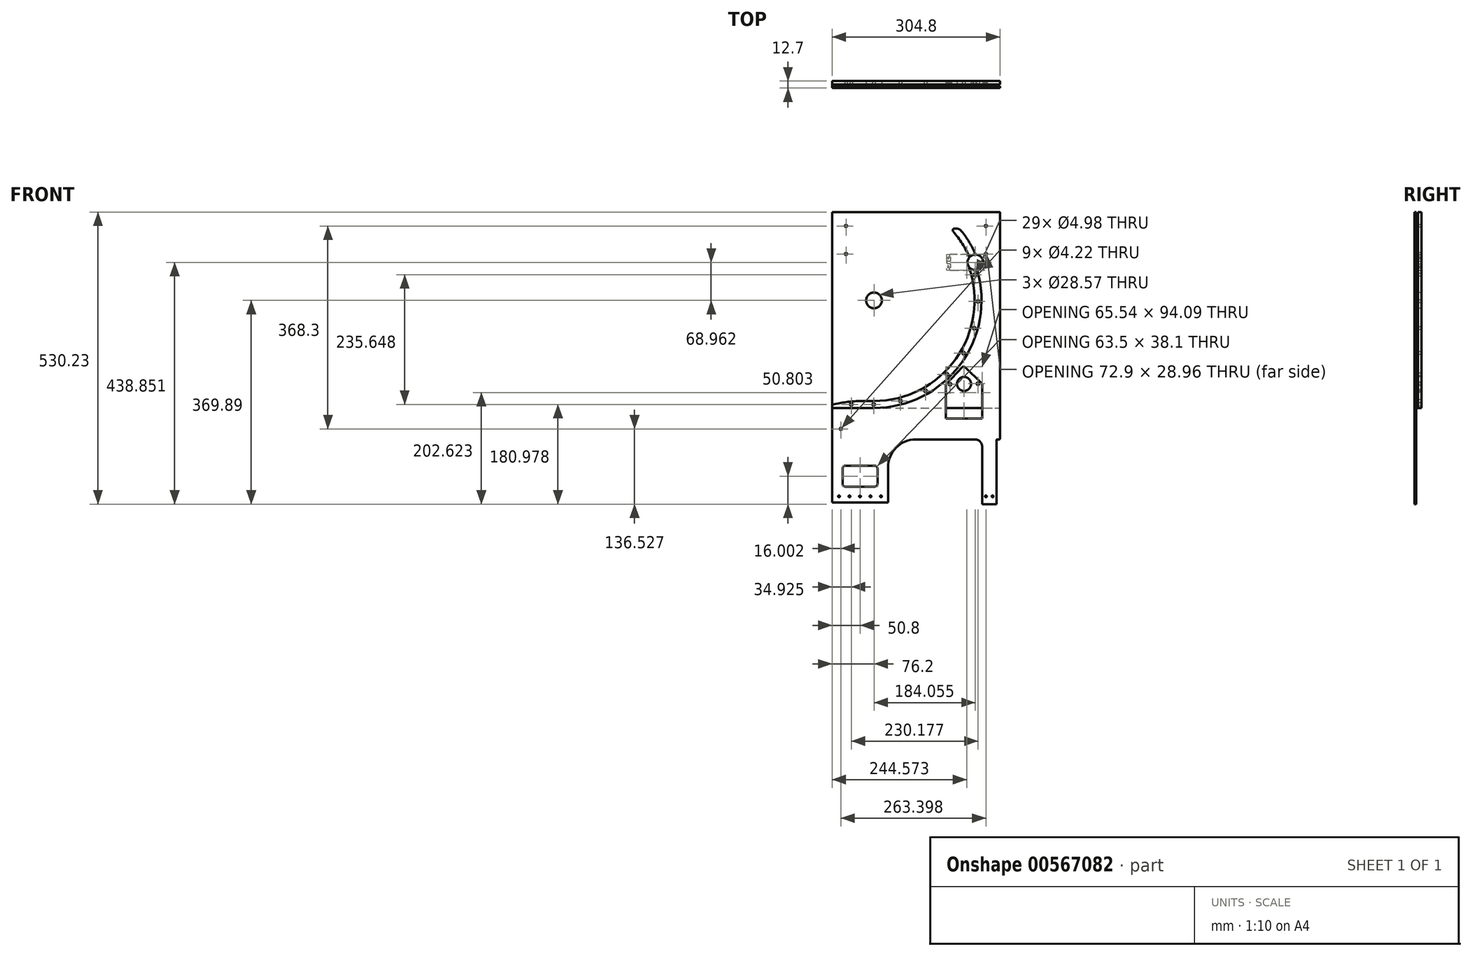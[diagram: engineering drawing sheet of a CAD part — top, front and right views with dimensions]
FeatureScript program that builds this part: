
annotation { "Feature Type Name" : "Feature", "Feature Type Description" : "" }
export const myFeature = defineFeature(function(context is Context, id is Id, definition is map)
    precondition{}
    {
        {
            var Q0;
            Q0=qCreatedBy(makeId("Front.planeOp"),FACE);
            var sketch = newSketch(context, id + "F0", { "sketchPlane" : qUnion([Q0])});
            skCircle(sketch, "E0", {"center": v(0, 0) * mm, "radius": 61.91 * mm, "construction": true});
            skArc(sketch, "E1", {"start": v(0, -182.56) * mm, "mid": v(148.63, -106.01) * mm, "end": v(172.62, 59.44) * mm});
            skLineSegment(sketch, "E2", {"start": v(228.6, -195.26) * mm, "end": v(228.6, 59.44) * mm, "construction": true});
            skLineSegment(sketch, "E3", {"start": v(228.6, 59.44) * mm, "end": v(172.62, 59.44) * mm});
            skLineSegment(sketch, "E4", {"start": v(0, 0) * mm, "end": v(182.56, 0) * mm, "construction": true});
            skLineSegment(sketch, "E5", {"start": v(0, 0) * mm, "end": v(172.62, 59.44) * mm, "construction": true});
            skLineSegment(sketch, "E6", {"start": v(209.55, -195.26) * mm, "end": v(209.55, 59.44) * mm, "construction": true});
            skPoint(sketch, "E7.middle", {"position": v(163.49, -151.68) * mm});
            skLineSegment(sketch, "E8.top", {"start": v(228.6, -195.26) * mm, "end": v(-76.2, -195.26) * mm});
            skLineSegment(sketch, "E8.right", {"start": v(-76.2, -188.91) * mm, "end": v(-76.2, -195.26) * mm});
            skLineSegment(sketch, "E9", {"start": v(0, -182.56) * mm, "end": v(-41.27, -182.56) * mm});
            skCircle(sketch, "E10", {"center": v(163.49, -151.68) * mm, "radius": 25.4 * mm, "construction": true});
            skLineSegment(sketch, "E11", {"start": v(130.72, -152.33) * mm, "end": v(162.84, -118.9) * mm, "construction": true});
            skLineSegment(sketch, "E12", {"start": v(162.84, -118.9) * mm, "end": v(196.26, -151.03) * mm, "construction": true});
            skLineSegment(sketch, "E13", {"start": v(196.26, -151.03) * mm, "end": v(164.14, -184.45) * mm, "construction": true});
            skLineSegment(sketch, "E14", {"start": v(164.14, -184.45) * mm, "end": v(130.72, -152.33) * mm, "construction": true});
            skLineSegment(sketch, "E15", {"start": v(162.84, -118.9) * mm, "end": v(164.14, -184.45) * mm, "construction": true});
            skCircle(sketch, "E16", {"center": v(183.04, 46.74) * mm, "radius": 2.49 * mm});
            skCircle(sketch, "E17.1.0", {"center": v(188.9, -2) * mm, "radius": 2.49 * mm});
            skCircle(sketch, "E17.2.0", {"center": v(182.01, -50.6) * mm, "radius": 2.49 * mm});
            skCircle(sketch, "E17.3.0", {"center": v(162.84, -95.77) * mm, "radius": 2.49 * mm});
            skCircle(sketch, "E17.4.0", {"center": v(132.67, -134.49) * mm, "radius": 2.49 * mm});
            skCircle(sketch, "E17.5.0", {"center": v(93.54, -164.13) * mm, "radius": 2.49 * mm});
            skCircle(sketch, "E17.6.0", {"center": v(48.1, -182.69) * mm, "radius": 2.49 * mm});
            skCircle(sketch, "E17.7.0", {"center": v(-0.58, -188.91) * mm, "radius": 2.49 * mm});
            skLineSegment(sketch, "E17.anchor1", {"start": v(0, 0) * mm, "end": v(183.04, 46.74) * mm, "construction": true});
            skLineSegment(sketch, "E17.anchor2", {"start": v(0, 0) * mm, "end": v(-0.58, -188.91) * mm, "construction": true});
            skLineSegment(sketch, "E18", {"start": v(130.72, -152.33) * mm, "end": v(130.72, -195.26) * mm, "construction": true});
            skLineSegment(sketch, "E19", {"start": v(196.26, -151.03) * mm, "end": v(196.26, -195.26) * mm, "construction": true});
            skCircle(sketch, "E20", {"center": v(-41.27, -188.91) * mm, "radius": 2.49 * mm});
            skLineSegment(sketch, "E21", {"start": v(-76.2, -188.91) * mm, "end": v(-41.27, -182.56) * mm});
            skArc(sketch, "E22.trimOffspring", {"start": v(0, -195.26) * mm, "mid": v(157.7, -115.16) * mm, "end": v(186, 59.44) * mm});
            skPoint(sketch, "E23.orphan", {"position": v(-76.2, -182.56) * mm});
            skSolve(sketch);
        }
        {
            var Q0;
            {var subQ1=sQuery(id+"F0.wireOp",EDGE,"E8.top");var subQ5=sQuery(id+"F0.wireOp",EDGE,"E8.right");var subQ6=makeQuery(id+"F0.imprint","INTERSECT",VERTEX,{"derivedFrom":[subQ1,subQ5]});Q0=makeQuery(id+"F0.imprint","IMPRINT",FACE,{"disambiguationData":[TD([[makeQuery(id+"F0.imprint","IMPRINT",EDGE,{"disambiguationData":[TD([[subQ6,1.0]])],"derivedFrom":subQ1}),-1.0]])]});}
            var Q1;
            {var subQ0=sQuery(id+"F0.wireOp",EDGE,"E1");Q1=makeQuery(id+"F0.imprint","IMPRINT",FACE,{"disambiguationData":[TD([[makeQuery(id+"F0.imprint","IMPRINT",EDGE,{"derivedFrom":subQ0}),-1.0]])]});}
            extrude(context, id + "F1", {"entities" : qUnion([Q0, Q1]), "depth" : 6.35 * mm, "offsetDistance" : 25.4 * mm});
        }
        {
            var Q0;
            {var subQ0=sQuery(id+"F0.wireOp",EDGE,"E1");Q0=makeQuery(id+"F0.imprint","IMPRINT",FACE,{"disambiguationData":[TD([[makeQuery(id+"F0.imprint","IMPRINT",EDGE,{"derivedFrom":subQ0}),-1.0]])]});}
            var sketch = newSketch(context, id + "F2", { "sketchPlane" : qUnion([Q0])});
            skCircle(sketch, "E24", {"center": v(0, 0) * mm, "radius": 14.29 * mm});
            skLineSegment(sketch, "E25.bottom", {"start": v(-76.2, -252.41) * mm, "end": v(228.6, -252.41) * mm});
            skLineSegment(sketch, "E25.top", {"start": v(-76.2, 160.34) * mm, "end": v(228.6, 160.34) * mm});
            skLineSegment(sketch, "E25.left", {"start": v(-76.2, -252.41) * mm, "end": v(-76.2, 160.34) * mm});
            skLineSegment(sketch, "E25.right", {"start": v(228.6, -252.41) * mm, "end": v(228.6, 160.34) * mm});
            skPoint(sketch, "E26.0", {"position": v(183.04, 46.74) * mm});
            skCircle(sketch, "E27.0", {"center": v(188.9, -2) * mm, "radius": 2.49 * mm});
            skCircle(sketch, "E27.1", {"center": v(183.04, 46.74) * mm, "radius": 2.49 * mm});
            skCircle(sketch, "E27.2", {"center": v(182.01, -50.6) * mm, "radius": 2.49 * mm});
            skCircle(sketch, "E27.3", {"center": v(162.84, -95.77) * mm, "radius": 2.49 * mm});
            skCircle(sketch, "E27.4", {"center": v(132.67, -134.49) * mm, "radius": 2.49 * mm});
            skCircle(sketch, "E27.5", {"center": v(93.54, -164.13) * mm, "radius": 2.49 * mm});
            skCircle(sketch, "E27.6", {"center": v(48.1, -182.69) * mm, "radius": 2.49 * mm});
            skCircle(sketch, "E27.7", {"center": v(-0.58, -188.91) * mm, "radius": 2.49 * mm});
            skCircle(sketch, "E27.8", {"center": v(-41.27, -188.91) * mm, "radius": 2.49 * mm});
            skCircle(sketch, "E28.0", {"center": v(163.49, -151.68) * mm, "radius": 25.4 * mm, "construction": true});
            skPoint(sketch, "E29.0", {"position": v(130.72, -152.33) * mm});
            skPoint(sketch, "E29.1", {"position": v(196.26, -151.03) * mm});
            skLineSegment(sketch, "E30", {"start": v(130.72, -152.33) * mm, "end": v(196.26, -151.03) * mm, "construction": true});
            skCircle(sketch, "E31", {"center": v(138.1, -152.18) * mm, "radius": 2.49 * mm});
            skCircle(sketch, "E32", {"center": v(188.88, -151.17) * mm, "radius": 2.49 * mm});
            skCircle(sketch, "E33", {"center": v(346.2, -207.96) * mm, "radius": 2.1 * mm});
            skLineSegment(sketch, "E34.bottom", {"start": v(-76.2, -195.26) * mm, "end": v(381, -195.26) * mm});
            skLineSegment(sketch, "E34.top", {"start": v(-76.2, -252.41) * mm, "end": v(381, -252.41) * mm});
            skLineSegment(sketch, "E34.left", {"start": v(-76.2, -195.26) * mm, "end": v(-76.2, -252.41) * mm});
            skLineSegment(sketch, "E34.right", {"start": v(381, -195.26) * mm, "end": v(381, -252.41) * mm});
            skCircle(sketch, "E35.0.1.0", {"center": v(346.2, -233.36) * mm, "radius": 2.1 * mm});
            skCircle(sketch, "E35.1.0.0", {"center": v(320.8, -207.96) * mm, "radius": 2.1 * mm});
            skCircle(sketch, "E35.1.1.0", {"center": v(320.8, -233.36) * mm, "radius": 2.1 * mm});
            skCircle(sketch, "E35.2.0.0", {"center": v(295.4, -207.96) * mm, "radius": 2.1 * mm});
            skCircle(sketch, "E35.2.1.0", {"center": v(295.4, -233.36) * mm, "radius": 2.1 * mm});
            skCircle(sketch, "E35.3.0.0", {"center": v(270, -207.96) * mm, "radius": 2.1 * mm});
            skCircle(sketch, "E35.3.1.0", {"center": v(270, -233.36) * mm, "radius": 2.1 * mm});
            skCircle(sketch, "E35.4.0.0", {"center": v(244.6, -207.96) * mm, "radius": 2.1 * mm});
            skCircle(sketch, "E35.4.1.0", {"center": v(244.6, -233.36) * mm, "radius": 2.1 * mm});
            skCircle(sketch, "E35.5.0.0", {"center": v(219.2, -207.96) * mm, "radius": 2.1 * mm});
            skCircle(sketch, "E35.5.1.0", {"center": v(219.2, -233.36) * mm, "radius": 2.1 * mm});
            skCircle(sketch, "E35.6.0.0", {"center": v(193.8, -207.96) * mm, "radius": 2.1 * mm});
            skCircle(sketch, "E35.6.1.0", {"center": v(193.8, -233.36) * mm, "radius": 2.1 * mm});
            skCircle(sketch, "E35.7.0.0", {"center": v(168.4, -207.96) * mm, "radius": 2.1 * mm});
            skCircle(sketch, "E35.7.1.0", {"center": v(168.4, -233.36) * mm, "radius": 2.1 * mm});
            skCircle(sketch, "E35.8.0.0", {"center": v(143, -207.96) * mm, "radius": 2.1 * mm});
            skCircle(sketch, "E35.8.1.0", {"center": v(143, -233.36) * mm, "radius": 2.1 * mm});
            skCircle(sketch, "E35.9.0.0", {"center": v(117.6, -207.96) * mm, "radius": 2.1 * mm});
            skCircle(sketch, "E35.9.1.0", {"center": v(117.6, -233.36) * mm, "radius": 2.1 * mm});
            skCircle(sketch, "E35.10.0.0", {"center": v(92.2, -207.96) * mm, "radius": 2.1 * mm});
            skCircle(sketch, "E35.10.1.0", {"center": v(92.2, -233.36) * mm, "radius": 2.1 * mm});
            skCircle(sketch, "E35.11.0.0", {"center": v(66.8, -207.96) * mm, "radius": 2.1 * mm});
            skCircle(sketch, "E35.11.1.0", {"center": v(66.8, -233.36) * mm, "radius": 2.1 * mm});
            skCircle(sketch, "E35.12.0.0", {"center": v(41.4, -207.96) * mm, "radius": 2.1 * mm});
            skCircle(sketch, "E35.12.1.0", {"center": v(41.4, -233.36) * mm, "radius": 2.1 * mm});
            skCircle(sketch, "E35.13.0.0", {"center": v(16, -207.96) * mm, "radius": 2.1 * mm});
            skCircle(sketch, "E35.13.1.0", {"center": v(16, -233.36) * mm, "radius": 2.1 * mm});
            skCircle(sketch, "E35.14.0.0", {"center": v(-9.4, -207.96) * mm, "radius": 2.1 * mm});
            skCircle(sketch, "E35.14.1.0", {"center": v(-9.4, -233.36) * mm, "radius": 2.1 * mm});
            skCircle(sketch, "E35.15.0.0", {"center": v(-34.8, -207.96) * mm, "radius": 2.1 * mm});
            skCircle(sketch, "E35.15.1.0", {"center": v(-34.8, -233.36) * mm, "radius": 2.1 * mm});
            skCircle(sketch, "E35.16.0.0", {"center": v(-60.2, -207.96) * mm, "radius": 2.1 * mm});
            skCircle(sketch, "E35.16.1.0", {"center": v(-60.2, -233.36) * mm, "radius": 2.1 * mm});
            skLineSegment(sketch, "E35.direction1", {"start": v(346.2, -207.96) * mm, "end": v(320.8, -207.96) * mm, "construction": true});
            skLineSegment(sketch, "E35.direction2", {"start": v(346.2, -207.96) * mm, "end": v(346.2, -233.36) * mm, "construction": true});
            skCircle(sketch, "E36", {"center": v(163.49, -151.68) * mm, "radius": 12.7 * mm});
            skLineSegment(sketch, "E37", {"start": v(-50.8, 160.34) * mm, "end": v(-50.8, -195.26) * mm, "construction": true});
            skCircle(sketch, "E38", {"center": v(-50.8, 84.14) * mm, "radius": 2.1 * mm});
            skCircle(sketch, "E39.0.1.0", {"center": v(-50.8, 134.94) * mm, "radius": 2.1 * mm});
            skLineSegment(sketch, "E39.direction1", {"start": v(-50.8, 84.14) * mm, "end": v(-50.8, 84.14) * mm});
            skLineSegment(sketch, "E39.direction2", {"start": v(-50.8, 84.14) * mm, "end": v(-50.8, 134.94) * mm, "construction": true});
            skLineSegment(sketch, "E40", {"start": v(76.2, 160.34) * mm, "end": v(76.2, -195.26) * mm, "construction": true});
            skCircle(sketch, "E41.MirrorC", {"center": v(203.2, 84.14) * mm, "radius": 2.1 * mm});
            skCircle(sketch, "E42.MirrorC", {"center": v(203.2, 134.94) * mm, "radius": 2.1 * mm});
            skLineSegment(sketch, "E43.MirrorCS", {"start": v(203.2, 84.14) * mm, "end": v(203.2, 134.94) * mm, "construction": true});
            skLineSegment(sketch, "E44.0", {"start": v(0, -182.56) * mm, "end": v(-41.27, -182.56) * mm});
            skSolve(sketch);
        }
        {
            var Q0;
            {var subQ3=sQuery(id+"F2.wireOp",EDGE,"E34.left");Q0=makeQuery(id+"F2.imprint","IMPRINT",FACE,{"disambiguationData":[TD([[makeQuery(id+"F2.imprint","IMPRINT",EDGE,{"derivedFrom":subQ3}),1.0]])]});}
            var Q1;
            Q1=makeQuery(id+"F2.imprint","IMPRINT",FACE,{"disambiguationData":[TD([[makeQuery(id+"F2.imprint","IMPRINT",EDGE,{"derivedFrom":sQuery(id+"F2.wireOp",EDGE,"E24")}),-1.0]])]});
            var Q2;
            Q2=makeQuery(id+"F2.imprint","IMPRINT",FACE,{"disambiguationData":[TD([[makeQuery(id+"F2.imprint","IMPRINT",EDGE,{"derivedFrom":sQuery(id+"F2.wireOp",EDGE,"E27.0")}),-1.0]])]});
            var Q3;
            {var subQ1=sQuery(id+"F0.wireOp",EDGE,"E21");var subQ2=makeQuery(id+"F0.imprint","INTERSECT",VERTEX,{"derivedFrom":[sQuery(id+"F0.wireOp",EDGE,"qDOghrOL-mCar-WwbD-ljMS-Sb26vS9t9zeY"),subQ1]});var subQ3=makeQuery(id+"F0.imprint","IMPRINT",EDGE,{"disambiguationData":[TD([[subQ2,1.0]])],"derivedFrom":subQ1});Q3=makeQuery(id+"F2.imprint","IMPRINT",FACE,{"disambiguationData":[TD([[makeQuery(id+"F2.imprint","IMPRINT",EDGE,{"derivedFrom":subQ3}),1.0]])]});}
            extrude(context, id + "F3", {"entities" : qUnion([Q0, Q1, Q2, Q3]), "oppositeDirection" : true, "depth" : 6.35 * mm, "offsetDistance" : 25.4 * mm});
        }
        {
            var Q0;
            Q0=makeQuery(id+"F1.opExtrude","CAP_FACE",FACE,{"disambiguationData":[OSD([sQuery(id+"F0.wireOp",EDGE,"E1"),sQuery(id+"F0.wireOp",EDGE,"E3"),sQuery(id+"F0.wireOp",EDGE,"E8.top"),sQuery(id+"F0.wireOp",EDGE,"E8.right"),sQuery(id+"F0.wireOp",EDGE,"E9"),sQuery(id+"F0.wireOp",EDGE,"E16"),sQuery(id+"F0.wireOp",EDGE,"E17.1.0"),sQuery(id+"F0.wireOp",EDGE,"E17.2.0"),sQuery(id+"F0.wireOp",EDGE,"E17.3.0"),sQuery(id+"F0.wireOp",EDGE,"E17.4.0"),sQuery(id+"F0.wireOp",EDGE,"E17.5.0"),sQuery(id+"F0.wireOp",EDGE,"E17.6.0"),sQuery(id+"F0.wireOp",EDGE,"E17.7.0"),sQuery(id+"F0.wireOp",EDGE,"qDOghrOL-mCar-WwbD-ljMS-Sb26vS9t9zeY"),sQuery(id+"F0.wireOp",EDGE,"E20")])],"isStart":false});
            var sketch = newSketch(context, id + "F4", { "sketchPlane" : qUnion([Q0])});
            skCircle(sketch, "E45.0", {"center": v(0, 0) * mm, "radius": 14.29 * mm});
            skCircle(sketch, "E46.0", {"center": v(162.84, -95.77) * mm, "radius": 2.49 * mm});
            skCircle(sketch, "E47.0", {"center": v(182.01, -50.6) * mm, "radius": 2.49 * mm});
            skCircle(sketch, "E47.1", {"center": v(188.9, -2) * mm, "radius": 2.49 * mm});
            skCircle(sketch, "E47.2", {"center": v(183.04, 46.74) * mm, "radius": 2.49 * mm});
            skCircle(sketch, "E47.3", {"center": v(132.67, -134.49) * mm, "radius": 2.49 * mm});
            skCircle(sketch, "E47.4", {"center": v(93.54, -164.13) * mm, "radius": 2.49 * mm});
            skCircle(sketch, "E47.5", {"center": v(48.1, -182.69) * mm, "radius": 2.49 * mm});
            skCircle(sketch, "E47.6", {"center": v(-0.58, -188.91) * mm, "radius": 2.49 * mm});
            skCircle(sketch, "E47.7", {"center": v(-41.27, -188.91) * mm, "radius": 2.49 * mm});
            skPoint(sketch, "E48.0", {"position": v(-76.2, 160.34) * mm});
            skLineSegment(sketch, "E49", {"start": v(-76.2, 160.34) * mm, "end": v(-76.2, -369.89) * mm});
            skPoint(sketch, "E50.0", {"position": v(228.6, -252.41) * mm});
            skLineSegment(sketch, "E51.bottom", {"start": v(-76.2, -369.89) * mm, "end": v(222.25, -369.89) * mm});
            skLineSegment(sketch, "E51.top", {"start": v(76.2, -252.41) * mm, "end": v(228.6, -252.41) * mm});
            skLineSegment(sketch, "E51.left", {"start": v(-76.2, -369.89) * mm, "end": v(-76.2, -252.41) * mm});
            skCircle(sketch, "E52.0", {"center": v(-60.2, -233.36) * mm, "radius": 2.1 * mm});
            skLineSegment(sketch, "E53", {"start": v(25.4, -369.89) * mm, "end": v(25.4, -303.21) * mm});
            skArc(sketch, "E54.filletArc", {"start": v(76.2, -252.41) * mm, "mid": v(40.28, -267.3) * mm, "end": v(25.4, -303.21) * mm});
            skPoint(sketch, "E55.0", {"position": v(76.2, 160.34) * mm});
            skLineSegment(sketch, "E56.0", {"start": v(-76.2, 160.34) * mm, "end": v(222.25, 160.34) * mm});
            skLineSegment(sketch, "E57.0", {"start": v(165.13, -121.1) * mm, "end": v(195.28, -150.09) * mm});
            skLineSegment(sketch, "E58.0", {"start": v(131.6, -151.4) * mm, "end": v(160.64, -121.2) * mm});
            skLineSegment(sketch, "E59.0", {"start": v(164.14, -184.45) * mm, "end": v(130.72, -152.33) * mm});
            skLineSegment(sketch, "E60.0", {"start": v(196.26, -151.03) * mm, "end": v(164.14, -184.45) * mm});
            skLineSegment(sketch, "E61.bottom", {"start": v(-76.2, -369.89) * mm, "end": v(25.4, -369.89) * mm});
            skLineSegment(sketch, "E61.top", {"start": v(-76.2, -344.49) * mm, "end": v(25.4, -344.49) * mm});
            skLineSegment(sketch, "E61.left", {"start": v(-76.2, -369.89) * mm, "end": v(-76.2, -344.49) * mm});
            skLineSegment(sketch, "E61.right", {"start": v(25.4, -369.89) * mm, "end": v(25.4, -344.49) * mm});
            skLineSegment(sketch, "E62", {"start": v(-76.2, -366.71) * mm, "end": v(25.4, -366.71) * mm});
            skLineSegment(sketch, "E63", {"start": v(-25.4, -366.71) * mm, "end": v(-25.4, -344.49) * mm, "construction": true});
            skCircle(sketch, "E64", {"center": v(-25.4, -355.6) * mm, "radius": 1.59 * mm});
            skLineSegment(sketch, "E65.direction1", {"start": v(-25.4, -355.6) * mm, "end": v(-6.35, -355.6) * mm, "construction": true});
            skCircle(sketch, "E66.MirrorC", {"center": v(-63.5, -355.6) * mm, "radius": 1.59 * mm});
            skCircle(sketch, "E67.MirrorC", {"center": v(-44.45, -355.6) * mm, "radius": 1.59 * mm});
            skLineSegment(sketch, "E68", {"start": v(130.72, -153.6) * mm, "end": v(130.72, -252.41) * mm});
            skLineSegment(sketch, "E69", {"start": v(196.26, -152.38) * mm, "end": v(196.26, -252.41) * mm});
            skPoint(sketch, "E70.visualSharp", {"position": v(162.84, -118.9) * mm});
            skArc(sketch, "E70.filletArc", {"start": v(165.13, -121.1) * mm, "mid": v(162.86, -120.22) * mm, "end": v(160.64, -121.2) * mm});
            skPoint(sketch, "E71.visualSharp", {"position": v(130.72, -152.33) * mm});
            skArc(sketch, "E71.filletArc", {"start": v(131.6, -151.4) * mm, "mid": v(130.95, -152.42) * mm, "end": v(130.72, -153.6) * mm});
            skPoint(sketch, "E72.visualSharp", {"position": v(196.26, -151.03) * mm});
            skArc(sketch, "E72.filletArc", {"start": v(196.26, -152.38) * mm, "mid": v(196, -151.13) * mm, "end": v(195.28, -150.09) * mm});
            skCircle(sketch, "E73.1", {"center": v(-50.8, 134.94) * mm, "radius": 2.1 * mm});
            skCircle(sketch, "E73.2", {"center": v(-50.8, 84.14) * mm, "radius": 2.1 * mm});
            skCircle(sketch, "E73.3", {"center": v(203.2, 84.14) * mm, "radius": 2.1 * mm});
            skCircle(sketch, "E73.5", {"center": v(203.2, 134.94) * mm, "radius": 2.1 * mm});
            skLineSegment(sketch, "E74", {"start": v(196.26, -252.41) * mm, "end": v(196.26, -369.89) * mm});
            skLineSegment(sketch, "E75", {"start": v(196.26, -366.71) * mm, "end": v(222.25, -366.71) * mm});
            skLineSegment(sketch, "E76", {"start": v(196.26, -344.49) * mm, "end": v(222.25, -344.49) * mm});
            skCircle(sketch, "E77.0.1.0", {"center": v(-6.35, -355.6) * mm, "radius": 1.59 * mm});
            skCircle(sketch, "E78.0.2.0", {"center": v(12.7, -355.6) * mm, "radius": 1.59 * mm});
            skCircle(sketch, "E79.0.12.0", {"center": v(203.2, -355.6) * mm, "radius": 1.59 * mm});
            skLineSegment(sketch, "E80", {"start": v(130.72, -214.31) * mm, "end": v(196.26, -214.31) * mm});
            skLineSegment(sketch, "E81.bottom", {"start": v(-57.15, -338.14) * mm, "end": v(6.35, -338.14) * mm});
            skLineSegment(sketch, "E81.top", {"start": v(-57.15, -300.04) * mm, "end": v(6.35, -300.04) * mm});
            skLineSegment(sketch, "E81.left", {"start": v(-57.15, -338.14) * mm, "end": v(-57.15, -300.04) * mm});
            skLineSegment(sketch, "E81.right", {"start": v(6.35, -338.14) * mm, "end": v(6.35, -300.04) * mm});
            skLineSegment(sketch, "E82", {"start": v(222.25, 160.34) * mm, "end": v(222.25, -369.89) * mm});
            skPoint(sketch, "E83.orphan", {"position": v(228.6, 160.34) * mm});
            skCircle(sketch, "E84", {"center": v(215.3, -355.6) * mm, "radius": 1.59 * mm});
            skLineSegment(sketch, "E85", {"start": v(203.2, -355.6) * mm, "end": v(196.26, -355.6) * mm, "construction": true});
            skLineSegment(sketch, "E86", {"start": v(215.3, -355.6) * mm, "end": v(222.25, -355.6) * mm, "construction": true});
            skLineSegment(sketch, "E87.bottom", {"start": v(222.25, 160.34) * mm, "end": v(228.6, 160.34) * mm});
            skLineSegment(sketch, "E87.top", {"start": v(222.25, -252.41) * mm, "end": v(228.6, -252.41) * mm});
            skLineSegment(sketch, "E87.left", {"start": v(222.25, 160.34) * mm, "end": v(222.25, -252.41) * mm});
            skLineSegment(sketch, "E87.right", {"start": v(228.6, 160.34) * mm, "end": v(228.6, -252.41) * mm});
            skSolve(sketch);
        }
        {
            var Q0;
            Q0=makeQuery(id+"F4.imprint","IMPRINT",FACE,{"disambiguationData":[TD([[makeQuery(id+"F4.imprint","IMPRINT",EDGE,{"derivedFrom":sQuery(id+"F4.wireOp",EDGE,"E46.0")}),-1.0]])]});
            var Q1;
            Q1=makeQuery(id+"F4.imprint","IMPRINT",FACE,{"disambiguationData":[TD([[makeQuery(id+"F4.imprint","IMPRINT",EDGE,{"derivedFrom":sQuery(id+"F4.wireOp",EDGE,"E45.0")}),-1.0]])]});
            var Q2;
            {var subQ5=sQuery(id+"F4.wireOp",EDGE,"E80");Q2=makeQuery(id+"F4.imprint","IMPRINT",FACE,{"disambiguationData":[TD([[makeQuery(id+"F4.imprint","IMPRINT",EDGE,{"derivedFrom":subQ5}),-1.0]])]});}
            var Q3;
            {var subQ5=sQuery(id+"F4.wireOp",EDGE,"E76");Q3=makeQuery(id+"F4.imprint","IMPRINT",FACE,{"disambiguationData":[TD([[makeQuery(id+"F4.imprint","IMPRINT",EDGE,{"derivedFrom":subQ5}),1.0]])]});}
            var Q4;
            {var subQ1=sQuery(id+"F4.wireOp",EDGE,"E61.top");Q4=makeQuery(id+"F4.imprint","IMPRINT",FACE,{"disambiguationData":[TD([[makeQuery(id+"F4.imprint","IMPRINT",EDGE,{"derivedFrom":subQ1}),-1.0]])]});}
            var Q5;
            {var subQ1=sQuery(id+"F4.wireOp",EDGE,"E75");Q5=makeQuery(id+"F4.imprint","IMPRINT",FACE,{"disambiguationData":[TD([[makeQuery(id+"F4.imprint","IMPRINT",EDGE,{"derivedFrom":subQ1}),1.0]])]});}
            var Q6;
            {var subQ5=sQuery(id+"F4.wireOp",EDGE,"E75");Q6=makeQuery(id+"F4.imprint","IMPRINT",FACE,{"disambiguationData":[TD([[makeQuery(id+"F4.imprint","IMPRINT",EDGE,{"derivedFrom":subQ5}),-1.0]])]});}
            var Q7;
            {var subQ0=sQuery(id+"F4.wireOp",EDGE,"E61.bottom");Q7=makeQuery(id+"F4.imprint","IMPRINT",FACE,{"disambiguationData":[TD([[makeQuery(id+"F4.imprint","IMPRINT",EDGE,{"derivedFrom":subQ0}),1.0]])]});}
            var Q8;
            Q8=makeQuery(id+"F4.imprint","IMPRINT",FACE,{"disambiguationData":[TD([[makeQuery(id+"F4.imprint","IMPRINT",EDGE,{"derivedFrom":sQuery(id+"F4.wireOp",EDGE,"E87.bottom")}),-1.0]])]});
            extrude(context, id + "F5", {"entities" : qUnion([Q0, Q1, Q2, Q3, Q4, Q5, Q6, Q7, Q8]), "oppositeDirection" : true, "depth" : 3.17 * mm, "offsetDistance" : 25.4 * mm});
        }
        {
            var Q0;
            Q0=makeQuery(id+"F1.opExtrude","SWEPT_EDGE",EDGE,{"disambiguationData":[OSD([sQuery(id+"F0.wireOp",EDGE,"E9"),sQuery(id+"F0.wireOp",EDGE,"E21")])]});
            fillet(context, id + "F6", {"entities" : qUnion([Q0]), "radius" : 269.2 * mm, "tangentPropagation" : true, "allowEdgeOverflow" : false});
        }
        {
            var Q0;
            Q0=makeQuery(id+"F5.opExtrude","SWEPT_EDGE",EDGE,{"disambiguationData":[OSD([sQuery(id+"F4.wireOp",EDGE,"E51.top"),sQuery(id+"F4.wireOp",EDGE,"E69"),sQuery(id+"F4.wireOp",EDGE,"E74")])]});
            fillet(context, id + "F7", {"entities" : qUnion([Q0]), "radius" : 12.7 * mm, "tangentPropagation" : true, "allowEdgeOverflow" : false});
        }
        {
            var Q0;
            Q0=makeQuery(id+"F5.opExtrude","SWEPT_EDGE",EDGE,{"disambiguationData":[OSD([sQuery(id+"F4.wireOp",EDGE,"E81.top"),sQuery(id+"F4.wireOp",EDGE,"E81.right")])]});
            var Q1;
            Q1=makeQuery(id+"F5.opExtrude","SWEPT_EDGE",EDGE,{"disambiguationData":[OSD([sQuery(id+"F4.wireOp",EDGE,"E81.top"),sQuery(id+"F4.wireOp",EDGE,"E81.left")])]});
            var Q2;
            Q2=makeQuery(id+"F5.opExtrude","SWEPT_EDGE",EDGE,{"disambiguationData":[OSD([sQuery(id+"F4.wireOp",EDGE,"E81.bottom"),sQuery(id+"F4.wireOp",EDGE,"E81.left")])]});
            var Q3;
            Q3=makeQuery(id+"F5.opExtrude","SWEPT_EDGE",EDGE,{"disambiguationData":[OSD([sQuery(id+"F4.wireOp",EDGE,"E81.bottom"),sQuery(id+"F4.wireOp",EDGE,"E81.right")])]});
            fillet(context, id + "F8", {"entities" : qUnion([Q0, Q1, Q2, Q3]), "radius" : 5.08 * mm, "tangentPropagation" : true, "allowEdgeOverflow" : false});
        }
        {
            var Q0;
            Q0=makeQuery(id+"F5.opExtrude","SWEPT_EDGE",EDGE,{"disambiguationData":[OSD([sQuery(id+"F4.wireOp",EDGE,"E87.top"),sQuery(id+"F4.wireOp",EDGE,"E87.right")])]});
            var Q1;
            Q1=makeQuery(id+"F5.opExtrude","SWEPT_EDGE",EDGE,{"disambiguationData":[OSD([sQuery(id+"F4.wireOp",EDGE,"E51.top"),sQuery(id+"F4.wireOp",EDGE,"E82"),sQuery(id+"F4.wireOp",EDGE,"E87.top"),sQuery(id+"F4.wireOp",EDGE,"E87.left")])]});
            fillet(context, id + "F9", {"entities" : qUnion([Q0, Q1]), "radius" : 1.27 * mm, "tangentPropagation" : true, "allowEdgeOverflow" : false});
        }
        {
            var Q0;
            Q0=makeQuery(id+"F5.opExtrude","CAP_FACE",FACE,{"disambiguationData":[OSD([sQuery(id+"F4.wireOp",EDGE,"E45.0"),sQuery(id+"F4.wireOp",EDGE,"E46.0"),sQuery(id+"F4.wireOp",EDGE,"E47.0"),sQuery(id+"F4.wireOp",EDGE,"E47.1"),sQuery(id+"F4.wireOp",EDGE,"E47.2"),sQuery(id+"F4.wireOp",EDGE,"E47.3"),sQuery(id+"F4.wireOp",EDGE,"E47.4"),sQuery(id+"F4.wireOp",EDGE,"E47.5"),sQuery(id+"F4.wireOp",EDGE,"E47.6"),sQuery(id+"F4.wireOp",EDGE,"E47.7"),sQuery(id+"F4.wireOp",EDGE,"E49"),sQuery(id+"F4.wireOp",EDGE,"E51.bottom"),sQuery(id+"F4.wireOp",EDGE,"E51.top"),sQuery(id+"F4.wireOp",EDGE,"E51.left"),sQuery(id+"F4.wireOp",EDGE,"E52.0"),sQuery(id+"F4.wireOp",EDGE,"E53"),sQuery(id+"F4.wireOp",EDGE,"E54.filletArc"),sQuery(id+"F4.wireOp",EDGE,"E56.0"),sQuery(id+"F4.wireOp",EDGE,"E57.0"),sQuery(id+"F4.wireOp",EDGE,"E58.0"),sQuery(id+"F4.wireOp",EDGE,"E61.bottom"),sQuery(id+"F4.wireOp",EDGE,"E61.left"),sQuery(id+"F4.wireOp",EDGE,"E61.right"),sQuery(id+"F4.wireOp",EDGE,"E64"),sQuery(id+"F4.wireOp",EDGE,"E66.MirrorC"),sQuery(id+"F4.wireOp",EDGE,"E67.MirrorC"),sQuery(id+"F4.wireOp",EDGE,"E68"),sQuery(id+"F4.wireOp",EDGE,"E69"),sQuery(id+"F4.wireOp",EDGE,"E70.filletArc"),sQuery(id+"F4.wireOp",EDGE,"E71.filletArc"),sQuery(id+"F4.wireOp",EDGE,"E72.filletArc"),sQuery(id+"F4.wireOp",EDGE,"E73.1"),sQuery(id+"F4.wireOp",EDGE,"E73.2"),sQuery(id+"F4.wireOp",EDGE,"E73.3"),sQuery(id+"F4.wireOp",EDGE,"E73.5"),sQuery(id+"F4.wireOp",EDGE,"E74"),sQuery(id+"F4.wireOp",EDGE,"E77.0.1.0"),sQuery(id+"F4.wireOp",EDGE,"E78.0.2.0"),sQuery(id+"F4.wireOp",EDGE,"E79.0.12.0"),sQuery(id+"F4.wireOp",EDGE,"E80"),sQuery(id+"F4.wireOp",EDGE,"E81.bottom"),sQuery(id+"F4.wireOp",EDGE,"E81.top"),sQuery(id+"F4.wireOp",EDGE,"E81.left"),sQuery(id+"F4.wireOp",EDGE,"E81.right"),sQuery(id+"F4.wireOp",EDGE,"E82"),sQuery(id+"F4.wireOp",EDGE,"E84"),sQuery(id+"F4.wireOp",EDGE,"E87.bottom"),sQuery(id+"F4.wireOp",EDGE,"E87.top"),sQuery(id+"F4.wireOp",EDGE,"E87.right")])],"isStart":true});
            var sketch = newSketch(context, id + "F10", { "sketchPlane" : qUnion([Q0])});
            skCircle(sketch, "E88", {"center": v(0, 0) * mm, "radius": 190.5 * mm});
            skCircle(sketch, "E89", {"center": v(0, 0) * mm, "radius": 202.6 * mm});
            skArc(sketch, "E90", {"start": v(178.39, 66.84) * mm, "mid": v(186.18, 63.3) * mm, "end": v(189.72, 71.08) * mm});
            skLineSegment(sketch, "E91", {"start": v(138.92, 130.35) * mm, "end": v(0, 0) * mm, "construction": true});
            skCircle(sketch, "E92.cCircle", {"center": v(184.06, 68.96) * mm, "radius": 4.76 * mm, "construction": true});
            skLineSegment(sketch, "E92.0", {"start": v(178.77, 70.48) * mm, "end": v(182.73, 74.3) * mm});
            skLineSegment(sketch, "E92.1", {"start": v(182.73, 74.3) * mm, "end": v(188.01, 72.78) * mm});
            skLineSegment(sketch, "E92.2", {"start": v(188.01, 72.78) * mm, "end": v(189.34, 67.44) * mm});
            skLineSegment(sketch, "E92.3", {"start": v(189.34, 67.44) * mm, "end": v(185.38, 63.63) * mm});
            skLineSegment(sketch, "E92.4", {"start": v(185.38, 63.63) * mm, "end": v(180.1, 65.14) * mm});
            skLineSegment(sketch, "E92.5", {"start": v(180.1, 65.14) * mm, "end": v(178.77, 70.48) * mm});
            skPoint(sketch, "E92.0.midPoint", {"position": v(180.75, 72.39) * mm});
            skLineSegment(sketch, "E93", {"start": v(138.92, 130.35) * mm, "end": v(155.1, 130.35) * mm});
            skCircle(sketch, "E94", {"center": v(184.06, 68.96) * mm, "radius": 14.29 * mm});
            skSolve(sketch);
        }
        {
            var Q0;
            {var subQ0=sQuery(id+"F10.wireOp",EDGE,"E90");Q0=makeQuery(id+"F10.imprint","IMPRINT",FACE,{"disambiguationData":[TD([[makeQuery(id+"F10.imprint","IMPRINT",EDGE,{"derivedFrom":subQ0}),1.0]])]});}
            var Q1;
            {var subQ0=sQuery(id+"F10.wireOp",EDGE,"E93");Q1=makeQuery(id+"F10.imprint","IMPRINT",FACE,{"disambiguationData":[TD([[makeQuery(id+"F10.imprint","IMPRINT",EDGE,{"derivedFrom":subQ0}),-1.0]])]});}
            extrude(context, id + "F11", {"entities" : qUnion([Q0, Q1]), "oppositeDirection" : true, "depth" : 6.35 * mm, "offsetDistance" : 25.4 * mm});
        }
        {
            var Q0;
            Q0=makeQuery(id+"F11.opExtrude","SWEPT_EDGE",EDGE,{"disambiguationData":[OSD([sQuery(id+"F10.wireOp",EDGE,"E89"),sQuery(id+"F10.wireOp",EDGE,"E93")])]});
            fillet(context, id + "F12", {"entities" : qUnion([Q0]), "radius" : 12.7 * mm, "tangentPropagation" : true, "allowEdgeOverflow" : false});
        }
        {
            var Q0;
            {var subQ0=sQuery(id+"F10.wireOp",EDGE,"E89");var subQ1=makeQuery(id+"F10.imprint","INTERSECT",VERTEX,{"derivedFrom":[subQ0,sQuery(id+"F10.wireOp",EDGE,"E90")]});Q0=makeQuery(id+"F10.imprint","IMPRINT",FACE,{"disambiguationData":[TD([[makeQuery(id+"F10.imprint","IMPRINT",EDGE,{"disambiguationData":[TD([[subQ1,1.0]])],"derivedFrom":subQ0}),-1.0]])]});}
            var Q1;
            {var subQ0=sQuery(id+"F10.wireOp",EDGE,"E88");var subQ1=makeQuery(id+"F10.imprint","INTERSECT",VERTEX,{"derivedFrom":[subQ0,sQuery(id+"F10.wireOp",EDGE,"E90")]});Q1=makeQuery(id+"F10.imprint","IMPRINT",FACE,{"disambiguationData":[TD([[makeQuery(id+"F10.imprint","IMPRINT",EDGE,{"disambiguationData":[TD([[subQ1,1.0]])],"derivedFrom":subQ0}),1.0]])]});}
            var Q2;
            {var subQ0=sQuery(id+"F10.wireOp",EDGE,"E90");Q2=makeQuery(id+"F10.imprint","IMPRINT",FACE,{"disambiguationData":[TD([[makeQuery(id+"F10.imprint","IMPRINT",EDGE,{"derivedFrom":subQ0}),1.0]])]});}
            var Q3;
            {var subQ0=sQuery(id+"F10.wireOp",EDGE,"E90");Q3=makeQuery(id+"F10.imprint","IMPRINT",FACE,{"disambiguationData":[TD([[makeQuery(id+"F10.imprint","IMPRINT",EDGE,{"derivedFrom":subQ0}),-1.0]])]});}
            var Q4;
            Q4=makeQuery(id+"F10.imprint","IMPRINT",FACE,{"disambiguationData":[TD([[makeQuery(id+"F10.imprint","IMPRINT",EDGE,{"derivedFrom":sQuery(id+"F10.wireOp",EDGE,"E92.0")}),-1.0]])]});
            var Q5;
            Q5=makeQuery(id+"F3.opExtrude","CAP_FACE",FACE,{"disambiguationData":[OSD([sQuery(id+"F2.wireOp",EDGE,"E24"),sQuery(id+"F2.wireOp",EDGE,"E25.top"),sQuery(id+"F2.wireOp",EDGE,"E25.left"),sQuery(id+"F2.wireOp",EDGE,"E25.right"),sQuery(id+"F2.wireOp",EDGE,"E27.0"),sQuery(id+"F2.wireOp",EDGE,"E27.1"),sQuery(id+"F2.wireOp",EDGE,"E27.2"),sQuery(id+"F2.wireOp",EDGE,"E27.3"),sQuery(id+"F2.wireOp",EDGE,"E27.4"),sQuery(id+"F2.wireOp",EDGE,"E27.5"),sQuery(id+"F2.wireOp",EDGE,"E27.6"),sQuery(id+"F2.wireOp",EDGE,"E27.7"),sQuery(id+"F2.wireOp",EDGE,"E27.8"),sQuery(id+"F2.wireOp",EDGE,"E31"),sQuery(id+"F2.wireOp",EDGE,"E32"),sQuery(id+"F2.wireOp",EDGE,"E34.top"),sQuery(id+"F2.wireOp",EDGE,"E34.left"),sQuery(id+"F2.wireOp",EDGE,"E35.5.0.0"),sQuery(id+"F2.wireOp",EDGE,"E35.5.1.0"),sQuery(id+"F2.wireOp",EDGE,"E35.6.0.0"),sQuery(id+"F2.wireOp",EDGE,"E35.6.1.0"),sQuery(id+"F2.wireOp",EDGE,"E35.7.0.0"),sQuery(id+"F2.wireOp",EDGE,"E35.7.1.0"),sQuery(id+"F2.wireOp",EDGE,"E35.8.0.0"),sQuery(id+"F2.wireOp",EDGE,"E35.8.1.0"),sQuery(id+"F2.wireOp",EDGE,"E35.9.0.0"),sQuery(id+"F2.wireOp",EDGE,"E35.9.1.0"),sQuery(id+"F2.wireOp",EDGE,"E35.10.0.0"),sQuery(id+"F2.wireOp",EDGE,"E35.10.1.0"),sQuery(id+"F2.wireOp",EDGE,"E35.11.0.0"),sQuery(id+"F2.wireOp",EDGE,"E35.11.1.0"),sQuery(id+"F2.wireOp",EDGE,"E35.12.0.0"),sQuery(id+"F2.wireOp",EDGE,"E35.12.1.0"),sQuery(id+"F2.wireOp",EDGE,"E35.13.0.0"),sQuery(id+"F2.wireOp",EDGE,"E35.13.1.0"),sQuery(id+"F2.wireOp",EDGE,"E35.14.0.0"),sQuery(id+"F2.wireOp",EDGE,"E35.14.1.0"),sQuery(id+"F2.wireOp",EDGE,"E35.15.0.0"),sQuery(id+"F2.wireOp",EDGE,"E35.15.1.0"),sQuery(id+"F2.wireOp",EDGE,"E35.16.0.0"),sQuery(id+"F2.wireOp",EDGE,"E35.16.1.0"),sQuery(id+"F2.wireOp",EDGE,"E36"),sQuery(id+"F2.wireOp",EDGE,"E38"),sQuery(id+"F2.wireOp",EDGE,"E39.0.1.0"),sQuery(id+"F2.wireOp",EDGE,"E41.MirrorC"),sQuery(id+"F2.wireOp",EDGE,"E42.MirrorC")])],"isStart":false});
            extrude(context, id + "F13", {"entities" : qUnion([Q0, Q1, Q2, Q3, Q4]), "operationType" : NewBodyOperationType.REMOVE, "endBound" : BoundingType.UP_TO_SURFACE, "oppositeDirection" : true, "depth" : 25.4 * mm, "endBoundEntityFace" : qUnion([Q5]), "offsetDistance" : 25.4 * mm});
        }
        {
            var Q0;
            Q0=makeQuery(id+"F3.opExtrude","CAP_FACE",FACE,{"disambiguationData":[OSD([sQuery(id+"F2.wireOp",EDGE,"E24"),sQuery(id+"F2.wireOp",EDGE,"E25.top"),sQuery(id+"F2.wireOp",EDGE,"E25.left"),sQuery(id+"F2.wireOp",EDGE,"E25.right"),sQuery(id+"F2.wireOp",EDGE,"E27.0"),sQuery(id+"F2.wireOp",EDGE,"E27.1"),sQuery(id+"F2.wireOp",EDGE,"E27.2"),sQuery(id+"F2.wireOp",EDGE,"E27.3"),sQuery(id+"F2.wireOp",EDGE,"E27.4"),sQuery(id+"F2.wireOp",EDGE,"E27.5"),sQuery(id+"F2.wireOp",EDGE,"E27.6"),sQuery(id+"F2.wireOp",EDGE,"E27.7"),sQuery(id+"F2.wireOp",EDGE,"E27.8"),sQuery(id+"F2.wireOp",EDGE,"E31"),sQuery(id+"F2.wireOp",EDGE,"E32"),sQuery(id+"F2.wireOp",EDGE,"E34.top"),sQuery(id+"F2.wireOp",EDGE,"E34.left"),sQuery(id+"F2.wireOp",EDGE,"E35.5.0.0"),sQuery(id+"F2.wireOp",EDGE,"E35.5.1.0"),sQuery(id+"F2.wireOp",EDGE,"E35.6.0.0"),sQuery(id+"F2.wireOp",EDGE,"E35.6.1.0"),sQuery(id+"F2.wireOp",EDGE,"E35.7.0.0"),sQuery(id+"F2.wireOp",EDGE,"E35.7.1.0"),sQuery(id+"F2.wireOp",EDGE,"E35.8.0.0"),sQuery(id+"F2.wireOp",EDGE,"E35.8.1.0"),sQuery(id+"F2.wireOp",EDGE,"E35.9.0.0"),sQuery(id+"F2.wireOp",EDGE,"E35.9.1.0"),sQuery(id+"F2.wireOp",EDGE,"E35.10.0.0"),sQuery(id+"F2.wireOp",EDGE,"E35.10.1.0"),sQuery(id+"F2.wireOp",EDGE,"E35.11.0.0"),sQuery(id+"F2.wireOp",EDGE,"E35.11.1.0"),sQuery(id+"F2.wireOp",EDGE,"E35.12.0.0"),sQuery(id+"F2.wireOp",EDGE,"E35.12.1.0"),sQuery(id+"F2.wireOp",EDGE,"E35.13.0.0"),sQuery(id+"F2.wireOp",EDGE,"E35.13.1.0"),sQuery(id+"F2.wireOp",EDGE,"E35.14.0.0"),sQuery(id+"F2.wireOp",EDGE,"E35.14.1.0"),sQuery(id+"F2.wireOp",EDGE,"E35.15.0.0"),sQuery(id+"F2.wireOp",EDGE,"E35.15.1.0"),sQuery(id+"F2.wireOp",EDGE,"E35.16.0.0"),sQuery(id+"F2.wireOp",EDGE,"E35.16.1.0"),sQuery(id+"F2.wireOp",EDGE,"E36"),sQuery(id+"F2.wireOp",EDGE,"E38"),sQuery(id+"F2.wireOp",EDGE,"E39.0.1.0"),sQuery(id+"F2.wireOp",EDGE,"E41.MirrorC"),sQuery(id+"F2.wireOp",EDGE,"E42.MirrorC")])],"isStart":false});
            var sketch = newSketch(context, id + "F14", { "sketchPlane" : qUnion([Q0])});
            skArc(sketch, "E95.0", {"start": v(-139.3, 83.44) * mm, "mid": v(-136.85, 81.35) * mm, "end": v(-138.53, 78.6) * mm});
            skLineSegment(sketch, "E95.1", {"start": v(-197.45, 83.44) * mm, "end": v(-139.3, 83.44) * mm});
            skLineSegment(sketch, "E95.2", {"start": v(-138.53, 78.6) * mm, "end": v(-138.53, 71.44) * mm});
            skLineSegment(sketch, "E95.3", {"start": v(-134.4, 71.44) * mm, "end": v(-138.53, 71.44) * mm});
            skArc(sketch, "E95.4", {"start": v(-134.4, 66.49) * mm, "mid": v(-131.92, 68.96) * mm, "end": v(-134.4, 71.44) * mm});
            skLineSegment(sketch, "E95.5", {"start": v(-138.53, 66.49) * mm, "end": v(-134.4, 66.49) * mm});
            skLineSegment(sketch, "E95.6", {"start": v(-138.53, 66.49) * mm, "end": v(-138.53, 59.32) * mm});
            skArc(sketch, "E95.7", {"start": v(-139.3, 54.48) * mm, "mid": v(-136.85, 56.57) * mm, "end": v(-138.53, 59.32) * mm});
            skArc(sketch, "E95.8", {"start": v(-197.45, 83.44) * mm, "mid": v(-199.9, 81.35) * mm, "end": v(-198.22, 78.6) * mm});
            skLineSegment(sketch, "E95.9", {"start": v(-198.22, 71.44) * mm, "end": v(-198.22, 78.6) * mm});
            skLineSegment(sketch, "E95.10", {"start": v(-202.35, 71.44) * mm, "end": v(-198.22, 71.44) * mm});
            skArc(sketch, "E95.11", {"start": v(-202.35, 66.49) * mm, "mid": v(-204.82, 68.96) * mm, "end": v(-202.35, 71.44) * mm});
            skLineSegment(sketch, "E95.12", {"start": v(-198.22, 66.49) * mm, "end": v(-202.35, 66.49) * mm});
            skLineSegment(sketch, "E95.13", {"start": v(-198.22, 59.32) * mm, "end": v(-198.22, 66.49) * mm});
            skArc(sketch, "E95.14", {"start": v(-197.45, 54.48) * mm, "mid": v(-199.9, 56.57) * mm, "end": v(-198.22, 59.32) * mm});
            skLineSegment(sketch, "E95.15", {"start": v(-139.3, 54.48) * mm, "end": v(-197.45, 54.48) * mm});
            skCircle(sketch, "E95.16", {"center": v(-202.03, 61.09) * mm, "radius": 1.35 * mm});
            skCircle(sketch, "E95.17", {"center": v(-202.03, 76.84) * mm, "radius": 1.35 * mm});
            skCircle(sketch, "E95.18", {"center": v(-134.72, 61.09) * mm, "radius": 1.35 * mm});
            skCircle(sketch, "E95.19", {"center": v(-134.72, 76.84) * mm, "radius": 1.35 * mm});
            skPoint(sketch, "E96.orphan", {"position": v(-268.94, 21.48) * mm});
            skCircle(sketch, "E97", {"center": v(-184.06, 68.96) * mm, "radius": 11.11 * mm});
            skLineSegment(sketch, "E98", {"start": v(-197.53, 50.67) * mm, "end": v(-170.58, 87.25) * mm, "construction": true});
            skSolve(sketch);
        }
        {
            var Q0;
            Q0 = qSketchRegion(id + "F14", true);
            var Q1;
            Q1=makeQuery(id+"F14.imprint","IMPRINT",FACE,{"disambiguationData":[TD([[makeQuery(id+"F14.imprint","IMPRINT",EDGE,{"derivedFrom":sQuery(id+"F14.wireOp",EDGE,"E97")}),1.0]])]});
            var Q2;
            Q2=makeQuery(id+"F3.opExtrude","CAP_FACE",FACE,{"disambiguationData":[OSD([sQuery(id+"F2.wireOp",EDGE,"E24"),sQuery(id+"F2.wireOp",EDGE,"E25.top"),sQuery(id+"F2.wireOp",EDGE,"E25.left"),sQuery(id+"F2.wireOp",EDGE,"E25.right"),sQuery(id+"F2.wireOp",EDGE,"E27.0"),sQuery(id+"F2.wireOp",EDGE,"E27.1"),sQuery(id+"F2.wireOp",EDGE,"E27.2"),sQuery(id+"F2.wireOp",EDGE,"E27.3"),sQuery(id+"F2.wireOp",EDGE,"E27.4"),sQuery(id+"F2.wireOp",EDGE,"E27.5"),sQuery(id+"F2.wireOp",EDGE,"E27.6"),sQuery(id+"F2.wireOp",EDGE,"E27.7"),sQuery(id+"F2.wireOp",EDGE,"E27.8"),sQuery(id+"F2.wireOp",EDGE,"E31"),sQuery(id+"F2.wireOp",EDGE,"E32"),sQuery(id+"F2.wireOp",EDGE,"E34.top"),sQuery(id+"F2.wireOp",EDGE,"E34.left"),sQuery(id+"F2.wireOp",EDGE,"E35.5.0.0"),sQuery(id+"F2.wireOp",EDGE,"E35.5.1.0"),sQuery(id+"F2.wireOp",EDGE,"E35.6.0.0"),sQuery(id+"F2.wireOp",EDGE,"E35.6.1.0"),sQuery(id+"F2.wireOp",EDGE,"E35.7.0.0"),sQuery(id+"F2.wireOp",EDGE,"E35.7.1.0"),sQuery(id+"F2.wireOp",EDGE,"E35.8.0.0"),sQuery(id+"F2.wireOp",EDGE,"E35.8.1.0"),sQuery(id+"F2.wireOp",EDGE,"E35.9.0.0"),sQuery(id+"F2.wireOp",EDGE,"E35.9.1.0"),sQuery(id+"F2.wireOp",EDGE,"E35.10.0.0"),sQuery(id+"F2.wireOp",EDGE,"E35.10.1.0"),sQuery(id+"F2.wireOp",EDGE,"E35.11.0.0"),sQuery(id+"F2.wireOp",EDGE,"E35.11.1.0"),sQuery(id+"F2.wireOp",EDGE,"E35.12.0.0"),sQuery(id+"F2.wireOp",EDGE,"E35.12.1.0"),sQuery(id+"F2.wireOp",EDGE,"E35.13.0.0"),sQuery(id+"F2.wireOp",EDGE,"E35.13.1.0"),sQuery(id+"F2.wireOp",EDGE,"E35.14.0.0"),sQuery(id+"F2.wireOp",EDGE,"E35.14.1.0"),sQuery(id+"F2.wireOp",EDGE,"E35.15.0.0"),sQuery(id+"F2.wireOp",EDGE,"E35.15.1.0"),sQuery(id+"F2.wireOp",EDGE,"E35.16.0.0"),sQuery(id+"F2.wireOp",EDGE,"E35.16.1.0"),sQuery(id+"F2.wireOp",EDGE,"E36"),sQuery(id+"F2.wireOp",EDGE,"E38"),sQuery(id+"F2.wireOp",EDGE,"E39.0.1.0"),sQuery(id+"F2.wireOp",EDGE,"E41.MirrorC"),sQuery(id+"F2.wireOp",EDGE,"E42.MirrorC")])],"isStart":true});
            extrude(context, id + "F15", {"entities" : qUnion([Q0, Q1]), "operationType" : NewBodyOperationType.REMOVE, "endBound" : BoundingType.UP_TO_SURFACE, "oppositeDirection" : true, "depth" : 25.4 * mm, "endBoundEntityFace" : qUnion([Q2]), "offsetDistance" : 25.4 * mm});
        }
        {
            var Q0;
            Q0=makeQuery(id+"F11.opExtrude","SWEPT_EDGE",EDGE,{"disambiguationData":[OSD([sQuery(id+"F10.wireOp",EDGE,"E88"),sQuery(id+"F10.wireOp",EDGE,"E93")])]});
            fillet(context, id + "F16", {"entities" : qUnion([Q0]), "radius" : 3.17 * mm, "tangentPropagation" : true, "allowEdgeOverflow" : false});
        }
    });
